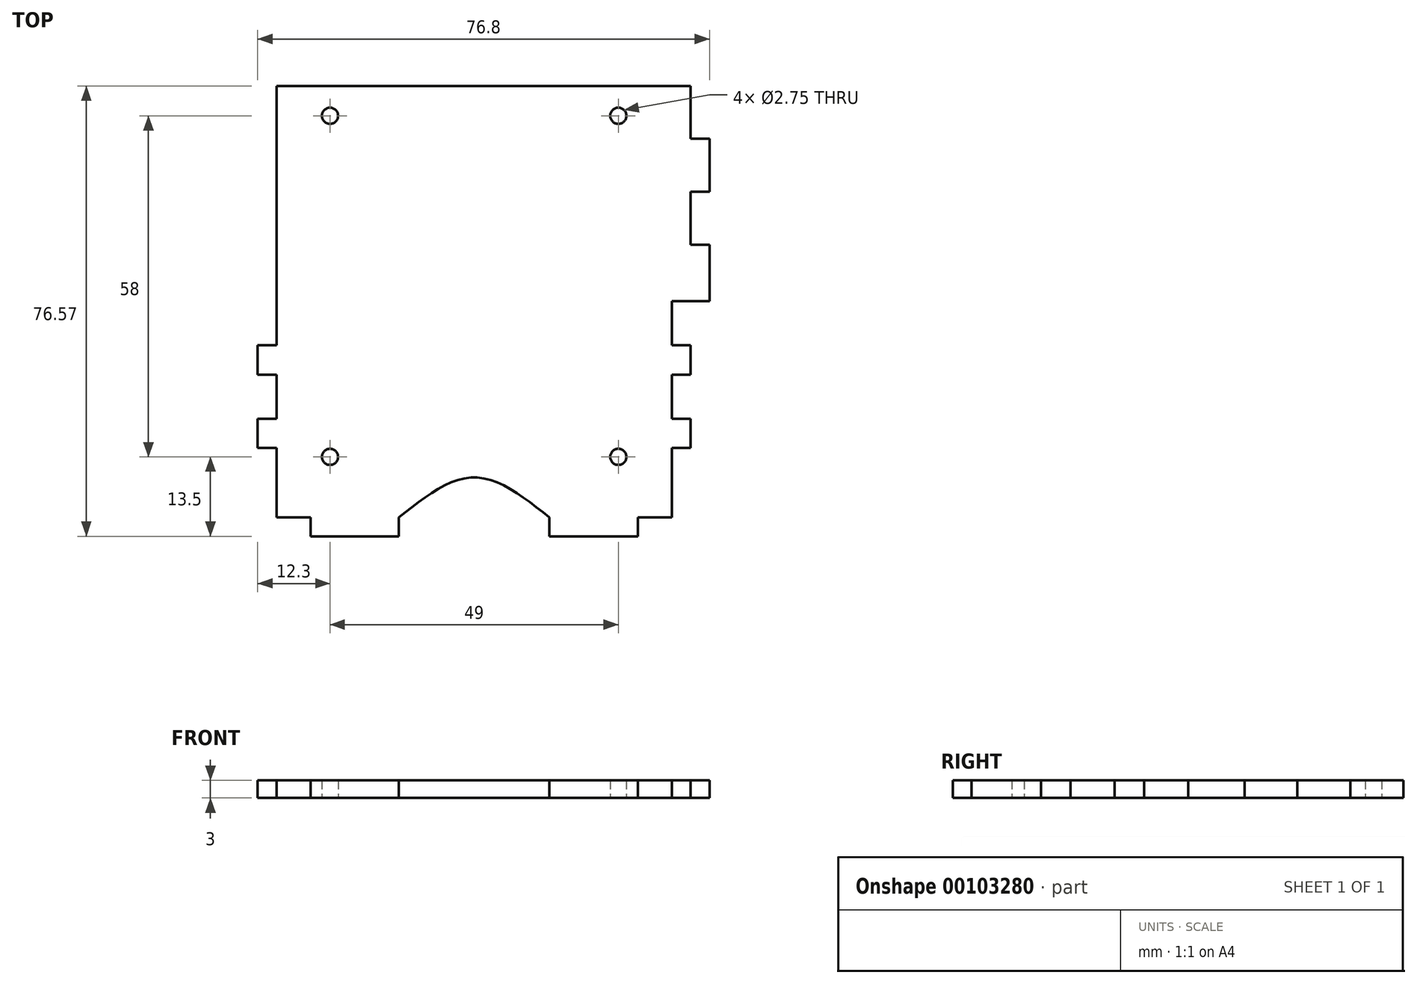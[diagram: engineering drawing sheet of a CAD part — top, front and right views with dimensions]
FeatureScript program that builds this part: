
annotation { "Feature Type Name" : "Feature", "Feature Type Description" : "" }
export const myFeature = defineFeature(function(context is Context, id is Id, definition is map)
    precondition{}
    {
        {
            var Q0;
            Q0=qCreatedBy(makeId("Top.planeOp"),FACE);
            var sketch = newSketch(context, id + "F0", { "sketchPlane" : qUnion([Q0])});
            skLineSegment(sketch, "E0.top", {"start": v(27.8, 34.07) * mm, "end": v(-27.8, 34.07) * mm});
            skPoint(sketch, "E0.middle", {"position": v(0, 0) * mm});
            skLineSegment(sketch, "E1", {"start": v(0, 0) * mm, "end": v(0, -32.5) * mm, "construction": true});
            skCircle(sketch, "E2", {"center": v(24.5, -29) * mm, "radius": 1.38 * mm});
            skCircle(sketch, "E3.MirrorC", {"center": v(-24.5, -29) * mm, "radius": 1.38 * mm});
            skCircle(sketch, "E4", {"center": v(-24.5, 29) * mm, "radius": 1.38 * mm});
            skCircle(sketch, "E5.MirrorC", {"center": v(24.5, 29) * mm, "radius": 1.38 * mm});
            skLineSegment(sketch, "E6", {"start": v(0, -32.5) * mm, "end": v(0, 32.5) * mm, "construction": true});
            skLineSegment(sketch, "E7", {"start": v(0, 0) * mm, "end": v(-27.8, 0) * mm, "construction": true});
            skLineSegment(sketch, "E8", {"start": v(0, 0) * mm, "end": v(27.8, 0) * mm, "construction": true});
            skLineSegment(sketch, "E9", {"start": v(-24.5, 29) * mm, "end": v(0, 29) * mm, "construction": true});
            skLineSegment(sketch, "E10", {"start": v(0, 29) * mm, "end": v(0, -24.3) * mm, "construction": true});
            skLineSegment(sketch, "E11", {"start": v(-27.8, -42.5) * mm, "end": v(-12.8, -42.5) * mm});
            skLineSegment(sketch, "E12", {"start": v(-12.8, -42.5) * mm, "end": v(-12.8, -39.3) * mm});
            skLineSegment(sketch, "E13.MirrorCS", {"start": v(12.8, -42.5) * mm, "end": v(12.8, -39.3) * mm});
            skLineSegment(sketch, "E14.MirrorCS", {"start": v(27.8, -42.5) * mm, "end": v(12.8, -42.5) * mm});
            skFitSpline(sketch, "E15", {"points": [v(-12.8, -39.3) * mm, v(0, -32.5) * mm, v(12.8, -39.3) * mm], "startDerivative": vector(25.6, 20.4) * mm, "endDerivative": vector(25.6, -20.4) * mm});
            skLineSegment(sketch, "E16", {"start": v(-27.8, -42.5) * mm, "end": v(-27.8, -39.3) * mm});
            skLineSegment(sketch, "E17", {"start": v(27.8, -39.3) * mm, "end": v(27.8, -42.5) * mm});
            skLineSegment(sketch, "E18", {"start": v(27.8, -42.5) * mm, "end": v(33.6, -42.5) * mm, "construction": true});
            skLineSegment(sketch, "E19", {"start": v(33.6, -42.5) * mm, "end": v(33.6, 25.07) * mm, "construction": true});
            skLineSegment(sketch, "E20", {"start": v(33.6, 34.07) * mm, "end": v(27.8, 34.07) * mm, "construction": true});
            skLineSegment(sketch, "E21", {"start": v(36.8, -2.5) * mm, "end": v(33.6, -2.5) * mm});
            skLineSegment(sketch, "E22", {"start": v(33.6, -2.5) * mm, "end": v(33.6, -10) * mm});
            skLineSegment(sketch, "E23", {"start": v(33.6, -10) * mm, "end": v(36.8, -10) * mm});
            skLineSegment(sketch, "E24", {"start": v(36.8, -10) * mm, "end": v(36.8, -15) * mm});
            skLineSegment(sketch, "E25", {"start": v(36.8, -15) * mm, "end": v(33.6, -15) * mm});
            skLineSegment(sketch, "E26", {"start": v(33.6, -15) * mm, "end": v(33.6, -22.5) * mm});
            skLineSegment(sketch, "E27", {"start": v(33.6, -22.5) * mm, "end": v(36.8, -22.5) * mm});
            skLineSegment(sketch, "E28", {"start": v(36.8, -22.5) * mm, "end": v(36.8, -27.5) * mm});
            skLineSegment(sketch, "E29", {"start": v(36.8, -27.5) * mm, "end": v(33.6, -27.5) * mm});
            skLineSegment(sketch, "E30", {"start": v(27.8, -42.5) * mm, "end": v(27.8, -39.3) * mm, "construction": true});
            skLineSegment(sketch, "E31", {"start": v(27.8, -39.3) * mm, "end": v(33.6, -39.3) * mm});
            skLineSegment(sketch, "E32", {"start": v(33.6, -39.3) * mm, "end": v(33.6, -27.5) * mm});
            skLineSegment(sketch, "E33", {"start": v(27.8, 34.07) * mm, "end": v(33.6, 34.07) * mm});
            skLineSegment(sketch, "E34.MirrorCS", {"start": v(-33.6, -42.5) * mm, "end": v(-33.6, 34.07) * mm, "construction": true});
            skLineSegment(sketch, "E35.MirrorCS", {"start": v(-33.6, -10) * mm, "end": v(-36.8, -10) * mm});
            skLineSegment(sketch, "E36.MirrorCS", {"start": v(-36.8, -10) * mm, "end": v(-36.8, -15) * mm});
            skLineSegment(sketch, "E37.MirrorCS", {"start": v(-36.8, -15) * mm, "end": v(-33.6, -15) * mm});
            skLineSegment(sketch, "E38.MirrorCS", {"start": v(-33.6, -22.5) * mm, "end": v(-36.8, -22.5) * mm});
            skLineSegment(sketch, "E39.MirrorCS", {"start": v(-36.8, -22.5) * mm, "end": v(-36.8, -27.5) * mm});
            skLineSegment(sketch, "E40.MirrorCS", {"start": v(-36.8, -27.5) * mm, "end": v(-33.6, -27.5) * mm});
            skLineSegment(sketch, "E41", {"start": v(-27.8, -42.5) * mm, "end": v(-27.8, -39.3) * mm, "construction": true});
            skLineSegment(sketch, "E42", {"start": v(-27.8, -39.3) * mm, "end": v(-33.6, -39.3) * mm});
            skLineSegment(sketch, "E43", {"start": v(-33.6, -39.3) * mm, "end": v(-33.6, -27.5) * mm});
            skLineSegment(sketch, "E44", {"start": v(-33.6, -22.5) * mm, "end": v(-33.6, -15) * mm});
            skLineSegment(sketch, "E45", {"start": v(-33.6, -10) * mm, "end": v(-33.6, 34.07) * mm});
            skLineSegment(sketch, "E46", {"start": v(-27.8, 34.07) * mm, "end": v(-33.6, 34.07) * mm});
            skLineSegment(sketch, "E47", {"start": v(33.6, 34.07) * mm, "end": v(36.8, 34.07) * mm, "construction": true});
            skLineSegment(sketch, "E48", {"start": v(36.8, 25.07) * mm, "end": v(40, 25.07) * mm});
            skLineSegment(sketch, "E49", {"start": v(40, 25.07) * mm, "end": v(40, 16.07) * mm});
            skLineSegment(sketch, "E50", {"start": v(40, 16.07) * mm, "end": v(36.8, 16.07) * mm});
            skLineSegment(sketch, "E51", {"start": v(36.8, 34.07) * mm, "end": v(36.8, 25.07) * mm});
            skLineSegment(sketch, "E52", {"start": v(33.6, 34.07) * mm, "end": v(36.8, 34.07) * mm});
            skLineSegment(sketch, "E53", {"start": v(36.8, 16.07) * mm, "end": v(36.8, 7.07) * mm});
            skLineSegment(sketch, "E54", {"start": v(36.8, 7.07) * mm, "end": v(40, 7.07) * mm});
            skLineSegment(sketch, "E55", {"start": v(40, 7.07) * mm, "end": v(40, -2.5) * mm});
            skLineSegment(sketch, "E56", {"start": v(40, -2.5) * mm, "end": v(36.8, -2.5) * mm});
            skSolve(sketch);
        }
        {
            var Q0;
            Q0=qSketchRegion(id+"F0",true);
            extrude(context, id + "F1", {"entities" : qUnion([Q0]), "endBound" : BoundingType.SYMMETRIC, "depth" : 3 * mm});
        }
    });
